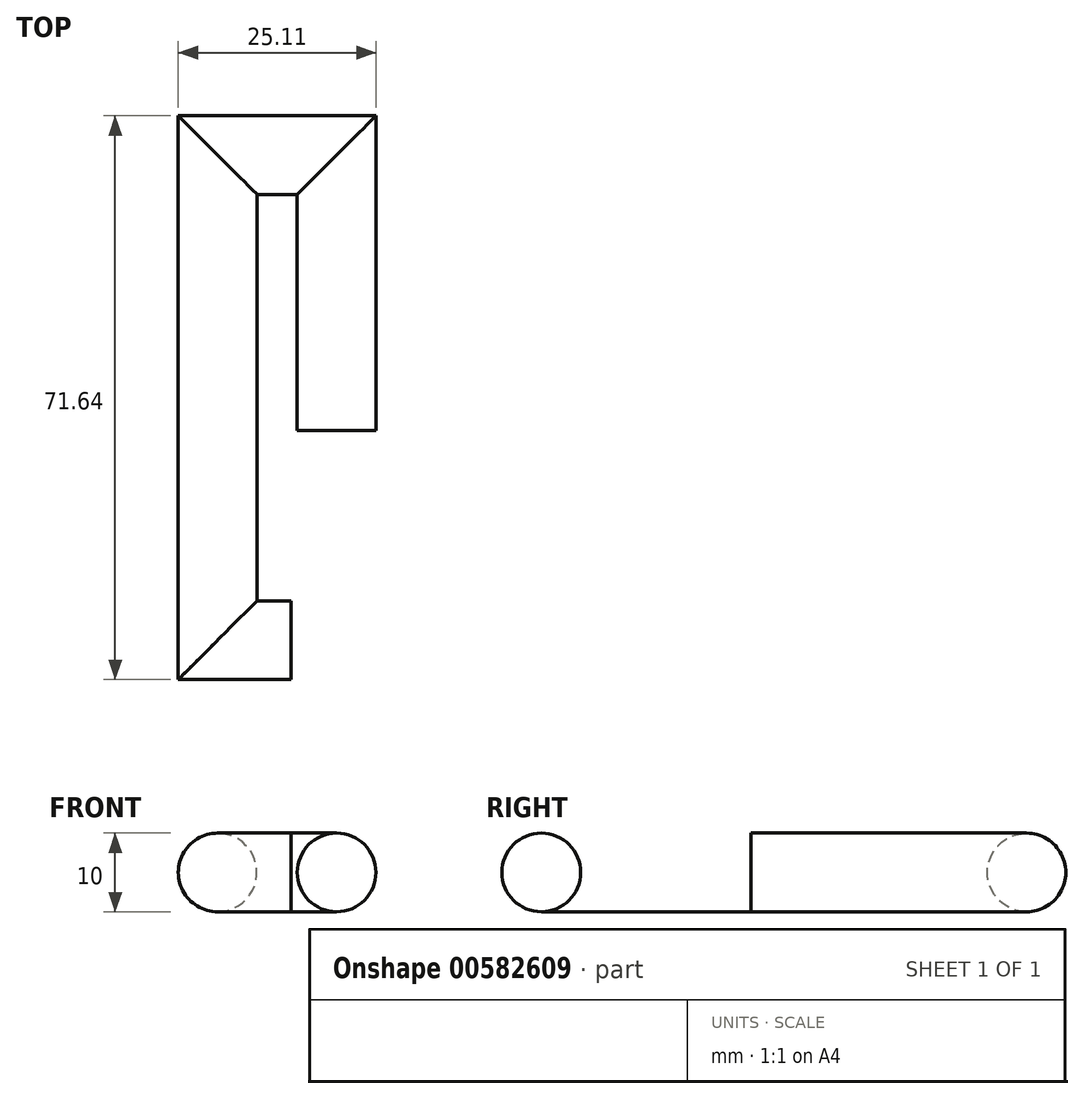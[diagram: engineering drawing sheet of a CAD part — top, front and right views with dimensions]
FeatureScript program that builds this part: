
annotation { "Feature Type Name" : "Feature", "Feature Type Description" : "" }
export const myFeature = defineFeature(function(context is Context, id is Id, definition is map)
    precondition{}
    {
        {
            var Q0;
            Q0=qCreatedBy(makeId("Front.planeOp"),FACE);
            var sketch = newSketch(context, id + "F0", { "sketchPlane" : qUnion([Q0])});
            skCircle(sketch, "E0", {"center": v(0, 0) * mm, "radius": 5 * mm});
            skSolve(sketch);
        }
        {
            var Q0;
            Q0=qCreatedBy(makeId("Top.planeOp"),FACE);
            var sketch = newSketch(context, id + "F1", { "sketchPlane" : qUnion([Q0])});
            skLineSegment(sketch, "E1", {"start": v(0, 0) * mm, "end": v(0, 35) * mm});
            skLineSegment(sketch, "E2", {"start": v(0, 35) * mm, "end": v(-15.1, 35) * mm});
            skLineSegment(sketch, "E3", {"start": v(-15.1, 35) * mm, "end": v(-15.1, -26.63) * mm});
            skLineSegment(sketch, "E4", {"start": v(-15.1, -26.63) * mm, "end": v(-5.77, -26.63) * mm});
            skLineSegment(sketch, "E5", {"start": v(-5.77, -26.63) * mm, "end": v(-5.77, 17.89) * mm});
            skSolve(sketch);
        }
        {
            var Q0;
            Q0=makeQuery(id+"F0.imprint","IMPRINT",FACE,{"disambiguationData":[TD([[makeQuery(id+"F0.imprint","IMPRINT",EDGE,{"derivedFrom":sQuery(id+"F0.wireOp",EDGE,"E0")}),1.0]])]});
            var Q1;
            Q1=sQuery(id+"F1.wireOp",EDGE,"E1");
            var Q2;
            Q2=sQuery(id+"F1.wireOp",EDGE,"E2");
            var Q3;
            Q3=sQuery(id+"F1.wireOp",EDGE,"E3");
            var Q4;
            Q4=sQuery(id+"F1.wireOp",EDGE,"E4");
            sweep(context, id + "F2", {"profiles" : qUnion([Q0]), "path" : qUnion([Q1, Q2, Q3, Q4])});
        }
    });
